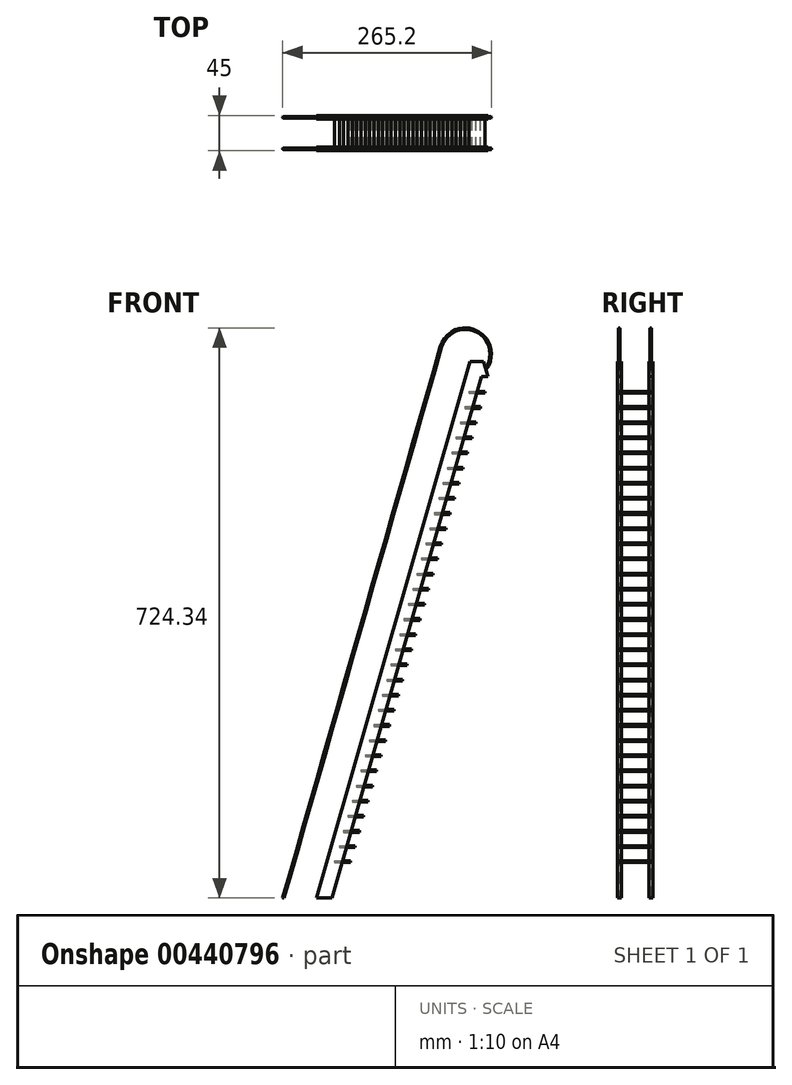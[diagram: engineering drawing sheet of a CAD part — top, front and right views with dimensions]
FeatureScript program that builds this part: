
annotation { "Feature Type Name" : "Feature", "Feature Type Description" : "" }
export const myFeature = defineFeature(function(context is Context, id is Id, definition is map)
    precondition{}
    {
        {
            var Q0;
            Q0=qCreatedBy(makeId("Front.planeOp"),FACE);
            cPlane(context, id + "F0", {"entities" : qUnion([Q0]), "cplaneType" : CPlaneType.OFFSET, "offset" : 20 * mm, "oppositeDirection" : true, "width" : 150 * mm, "height" : 150 * mm});
        }
        {
            var Q0;
            Q0=qCreatedBy(makeId("Front.planeOp"),FACE);
            var sketch = newSketch(context, id + "F1", { "sketchPlane" : qUnion([Q0])});
            skLineSegment(sketch, "E0.bottom", {"start": v(100, -350) * mm, "end": v(-100, -350) * mm});
            skLineSegment(sketch, "E0.top", {"start": v(100, 350) * mm, "end": v(-100, 350) * mm});
            skLineSegment(sketch, "E0.left", {"start": v(100, -350) * mm, "end": v(100, 350) * mm});
            skLineSegment(sketch, "E0.right", {"start": v(-100, -350) * mm, "end": v(-100, 350) * mm});
            skPoint(sketch, "E0.middle", {"position": v(0, 0) * mm});
            skSolve(sketch);
        }
        {
            var Q0;
            Q0=qCreatedBy(id+"F0.planeOp",FACE);
            var sketch = newSketch(context, id + "F2", { "sketchPlane" : qUnion([Q0])});
            skLineSegment(sketch, "E1.0", {"start": v(-100, -350) * mm, "end": v(-100, 350) * mm, "construction": true});
            skLineSegment(sketch, "E2.0", {"start": v(100, -350) * mm, "end": v(100, 350) * mm, "construction": true});
            skLineSegment(sketch, "E3.0", {"start": v(100, 350) * mm, "end": v(-100, 350) * mm, "construction": true});
            skLineSegment(sketch, "E4.0", {"start": v(100, -350) * mm, "end": v(-100, -350) * mm, "construction": true});
            skLineSegment(sketch, "E5", {"start": v(100, 350) * mm, "end": v(-100, -350) * mm});
            skLineSegment(sketch, "E6.0", {"start": v(128.85, 341.76) * mm, "end": v(-68.8, -350) * mm});
            skLineSegment(sketch, "E7", {"start": v(-100, -350) * mm, "end": v(-68.8, -350) * mm});
            skArc(sketch, "E8", {"start": v(157.14, 322.29) * mm, "mid": v(145.06, 370.15) * mm, "end": v(100, 350) * mm});
            skSolve(sketch);
        }
        {
            var Q0;
            Q0=qCreatedBy(makeId("Top.planeOp"),FACE);
            var Q1;
            Q1=sQuery(id+"F2.wireOp",VERTEX,"E7.start");
            cPlane(context, id + "F3", {"entities" : qUnion([Q0, Q1]), "cplaneType" : CPlaneType.PLANE_POINT, "offset" : 340.5 * mm, "oppositeDirection" : true, "width" : 150 * mm, "height" : 150 * mm});
        }
        {
            var Q0;
            Q0=qCreatedBy(id+"F3.planeOp",FACE);
            var sketch = newSketch(context, id + "F4", { "sketchPlane" : qUnion([Q0])});
            skPoint(sketch, "E9.0", {"position": v(-100, 20) * mm});
            skCircle(sketch, "E10", {"center": v(-100, 20) * mm, "radius": 1 * mm});
            skSolve(sketch);
        }
        {
            var Q0;
            Q0=makeQuery(id+"F4.imprint","IMPRINT",FACE,{"disambiguationData":[TD([[makeQuery(id+"F4.imprint","IMPRINT",EDGE,{"derivedFrom":sQuery(id+"F4.wireOp",EDGE,"E10")}),1.0]])]});
            var Q1;
            Q1=sQuery(id+"F2.wireOp",EDGE,"E5");
            var Q2;
            Q2=sQuery(id+"F2.wireOp",EDGE,"E8");
            sweep(context, id + "F5", {"profiles" : qUnion([Q0]), "path" : qUnion([Q1, Q2])});
        }
        {
            var Q0;
            Q0=qCreatedBy(id+"F0.planeOp",FACE);
            var sketch = newSketch(context, id + "F6", { "sketchPlane" : qUnion([Q0])});
            skPoint(sketch, "E11.0", {"position": v(157.14, 322.29) * mm});
            skPoint(sketch, "E12.0", {"position": v(100, 350) * mm});
            skPoint(sketch, "E13.0", {"position": v(-100, -350) * mm});
            skLineSegment(sketch, "E14.0", {"start": v(144.08, 322.29) * mm, "end": v(-48, -350) * mm});
            skLineSegment(sketch, "E15", {"start": v(157.14, 322.29) * mm, "end": v(144.08, 322.29) * mm});
            skLineSegment(sketch, "E16.0", {"start": v(100, -350) * mm, "end": v(-100, -350) * mm, "construction": true});
            skSolve(sketch);
        }
        {
            var Q0;
            Q0=qCreatedBy(id+"F3.planeOp",FACE);
            var sketch = newSketch(context, id + "F7", { "sketchPlane" : qUnion([Q0])});
            skLineSegment(sketch, "E17.bottom", {"start": v(-38, 22.5) * mm, "end": v(-58, 22.5) * mm});
            skLineSegment(sketch, "E17.top", {"start": v(-38, 17.5) * mm, "end": v(-58, 17.5) * mm});
            skLineSegment(sketch, "E17.left", {"start": v(-38, 22.5) * mm, "end": v(-38, 17.5) * mm});
            skLineSegment(sketch, "E17.right", {"start": v(-58, 22.5) * mm, "end": v(-58, 17.5) * mm});
            skPoint(sketch, "E17.middle", {"position": v(-48, 20) * mm});
            skSolve(sketch);
        }
        {
            var Q0;
            Q0 = qSketchRegion(id + "F7", true);
            var Q1;
            Q1=sQuery(id+"F6.wireOp",EDGE,"E14.0");
            var Q2;
            Q2=sQuery(id+"F6.wireOp",EDGE,"E15");
            sweep(context, id + "F8", {"profiles" : qUnion([Q0]), "path" : qUnion([Q1, Q2])});
        }
        {
            var Q0;
            Q0=makeQuery(id+"F5.opSweep","SWEPT_BODY",BODY,{"disambiguationData":[OSD([sQuery(id+"F2.wireOp",EDGE,"E8"),sQuery(id+"F4.wireOp",EDGE,"E10")])]});
            var Q1;
            Q1=makeQuery(id+"F8.opSweep","SWEPT_BODY",BODY,{"disambiguationData":[OSD([sQuery(id+"F6.wireOp",EDGE,"E15"),sQuery(id+"F7.wireOp",EDGE,"E17.bottom"),sQuery(id+"F7.wireOp",EDGE,"E17.top"),sQuery(id+"F7.wireOp",EDGE,"E17.left"),sQuery(id+"F7.wireOp",EDGE,"E17.right")])]});
            var Q2;
            Q2=makeQuery(id+"F1.imprint","IMPRINT",FACE,{"disambiguationData":[TD([[makeQuery(id+"F1.imprint","IMPRINT",EDGE,{"derivedFrom":sQuery(id+"F1.wireOp",EDGE,"E0.bottom")}),-1.0]])]});
            mirror(context, id + "F9", {"entities" : qUnion([Q0, Q1]), "mirrorPlane" : qUnion([Q2])});
        }
        {
            var Q0;
            Q0=qCreatedBy(id+"F0.planeOp",FACE);
            var sketch = newSketch(context, id + "F10", { "sketchPlane" : qUnion([Q0])});
            skLineSegment(sketch, "E18.0", {"start": v(144.08, 322.29) * mm, "end": v(-48, -350) * mm, "construction": true});
            skLineSegment(sketch, "E19.bottom", {"start": v(135.84, 293.44) * mm, "end": v(155.84, 293.44) * mm});
            skLineSegment(sketch, "E19.top", {"start": v(135.84, 291.44) * mm, "end": v(155.84, 291.44) * mm});
            skLineSegment(sketch, "E19.left", {"start": v(135.84, 293.44) * mm, "end": v(135.84, 291.44) * mm});
            skLineSegment(sketch, "E19.right", {"start": v(155.84, 293.44) * mm, "end": v(155.84, 291.44) * mm});
            skLineSegment(sketch, "E20.bottom", {"start": v(130.35, 274.21) * mm, "end": v(150.35, 274.21) * mm});
            skLineSegment(sketch, "E20.top", {"start": v(130.35, 272.21) * mm, "end": v(150.35, 272.21) * mm});
            skLineSegment(sketch, "E20.left", {"start": v(130.35, 274.21) * mm, "end": v(130.35, 272.21) * mm});
            skLineSegment(sketch, "E20.right", {"start": v(150.35, 274.21) * mm, "end": v(150.35, 272.21) * mm});
            skLineSegment(sketch, "E21.bottom", {"start": v(124.85, 254.98) * mm, "end": v(144.85, 254.98) * mm});
            skLineSegment(sketch, "E21.top", {"start": v(124.85, 252.98) * mm, "end": v(144.85, 252.98) * mm});
            skLineSegment(sketch, "E21.left", {"start": v(124.85, 254.98) * mm, "end": v(124.85, 252.98) * mm});
            skLineSegment(sketch, "E21.right", {"start": v(144.85, 254.98) * mm, "end": v(144.85, 252.98) * mm});
            skLineSegment(sketch, "E22.bottom", {"start": v(119.36, 235.75) * mm, "end": v(139.36, 235.75) * mm});
            skLineSegment(sketch, "E22.top", {"start": v(119.36, 233.75) * mm, "end": v(139.36, 233.75) * mm});
            skLineSegment(sketch, "E22.left", {"start": v(119.36, 235.75) * mm, "end": v(119.36, 233.75) * mm});
            skLineSegment(sketch, "E22.right", {"start": v(139.36, 235.75) * mm, "end": v(139.36, 233.75) * mm});
            skLineSegment(sketch, "E23.bottom", {"start": v(113.86, 216.52) * mm, "end": v(133.86, 216.52) * mm});
            skLineSegment(sketch, "E23.top", {"start": v(113.86, 214.52) * mm, "end": v(133.86, 214.52) * mm});
            skLineSegment(sketch, "E23.left", {"start": v(113.86, 216.52) * mm, "end": v(113.86, 214.52) * mm});
            skLineSegment(sketch, "E23.right", {"start": v(133.86, 216.52) * mm, "end": v(133.86, 214.52) * mm});
            skLineSegment(sketch, "E24.bottom", {"start": v(108.37, 197.29) * mm, "end": v(128.37, 197.29) * mm});
            skLineSegment(sketch, "E24.top", {"start": v(108.37, 195.29) * mm, "end": v(128.37, 195.29) * mm});
            skLineSegment(sketch, "E24.left", {"start": v(108.37, 197.29) * mm, "end": v(108.37, 195.29) * mm});
            skLineSegment(sketch, "E24.right", {"start": v(128.37, 197.29) * mm, "end": v(128.37, 195.29) * mm});
            skLineSegment(sketch, "E25.bottom", {"start": v(102.87, 178.06) * mm, "end": v(122.87, 178.06) * mm});
            skLineSegment(sketch, "E25.top", {"start": v(102.87, 176.06) * mm, "end": v(122.87, 176.06) * mm});
            skLineSegment(sketch, "E25.left", {"start": v(102.87, 178.06) * mm, "end": v(102.87, 176.06) * mm});
            skLineSegment(sketch, "E25.right", {"start": v(122.87, 178.06) * mm, "end": v(122.87, 176.06) * mm});
            skLineSegment(sketch, "E26.bottom", {"start": v(97.38, 158.83) * mm, "end": v(117.38, 158.83) * mm});
            skLineSegment(sketch, "E26.top", {"start": v(97.38, 156.83) * mm, "end": v(117.38, 156.83) * mm});
            skLineSegment(sketch, "E26.left", {"start": v(97.38, 158.83) * mm, "end": v(97.38, 156.83) * mm});
            skLineSegment(sketch, "E26.right", {"start": v(117.38, 158.83) * mm, "end": v(117.38, 156.83) * mm});
            skLineSegment(sketch, "E27.bottom", {"start": v(91.89, 139.6) * mm, "end": v(111.89, 139.6) * mm});
            skLineSegment(sketch, "E27.top", {"start": v(91.89, 137.6) * mm, "end": v(111.89, 137.6) * mm});
            skLineSegment(sketch, "E27.left", {"start": v(91.89, 139.6) * mm, "end": v(91.89, 137.6) * mm});
            skLineSegment(sketch, "E27.right", {"start": v(111.89, 139.6) * mm, "end": v(111.89, 137.6) * mm});
            skLineSegment(sketch, "E28.bottom", {"start": v(86.4, 120.37) * mm, "end": v(106.4, 120.37) * mm});
            skLineSegment(sketch, "E28.top", {"start": v(86.4, 118.37) * mm, "end": v(106.4, 118.37) * mm});
            skLineSegment(sketch, "E28.left", {"start": v(86.4, 120.37) * mm, "end": v(86.4, 118.37) * mm});
            skLineSegment(sketch, "E28.right", {"start": v(106.4, 120.37) * mm, "end": v(106.4, 118.37) * mm});
            skLineSegment(sketch, "E29.bottom", {"start": v(80.9, 101.14) * mm, "end": v(100.9, 101.14) * mm});
            skLineSegment(sketch, "E29.top", {"start": v(80.9, 99.14) * mm, "end": v(100.9, 99.14) * mm});
            skLineSegment(sketch, "E29.left", {"start": v(80.9, 101.14) * mm, "end": v(80.9, 99.14) * mm});
            skLineSegment(sketch, "E29.right", {"start": v(100.9, 101.14) * mm, "end": v(100.9, 99.14) * mm});
            skLineSegment(sketch, "E30.bottom", {"start": v(75.4, 81.9) * mm, "end": v(95.4, 81.9) * mm});
            skLineSegment(sketch, "E30.top", {"start": v(75.4, 79.9) * mm, "end": v(95.4, 79.9) * mm});
            skLineSegment(sketch, "E30.left", {"start": v(75.4, 81.9) * mm, "end": v(75.4, 79.9) * mm});
            skLineSegment(sketch, "E30.right", {"start": v(95.4, 81.9) * mm, "end": v(95.4, 79.9) * mm});
            skLineSegment(sketch, "E31.bottom", {"start": v(69.9, 62.68) * mm, "end": v(89.9, 62.68) * mm});
            skLineSegment(sketch, "E31.top", {"start": v(69.9, 60.68) * mm, "end": v(89.9, 60.68) * mm});
            skLineSegment(sketch, "E31.left", {"start": v(69.9, 62.68) * mm, "end": v(69.9, 60.68) * mm});
            skLineSegment(sketch, "E31.right", {"start": v(89.9, 62.68) * mm, "end": v(89.9, 60.68) * mm});
            skLineSegment(sketch, "E32.bottom", {"start": v(64.41, 43.45) * mm, "end": v(84.41, 43.45) * mm});
            skLineSegment(sketch, "E32.top", {"start": v(64.41, 41.45) * mm, "end": v(84.41, 41.45) * mm});
            skLineSegment(sketch, "E32.left", {"start": v(64.41, 43.45) * mm, "end": v(64.41, 41.45) * mm});
            skLineSegment(sketch, "E32.right", {"start": v(84.41, 43.45) * mm, "end": v(84.41, 41.45) * mm});
            skLineSegment(sketch, "E33.bottom", {"start": v(58.92, 24.21) * mm, "end": v(78.92, 24.21) * mm});
            skLineSegment(sketch, "E33.top", {"start": v(58.92, 22.21) * mm, "end": v(78.92, 22.21) * mm});
            skLineSegment(sketch, "E33.left", {"start": v(58.92, 24.21) * mm, "end": v(58.92, 22.21) * mm});
            skLineSegment(sketch, "E33.right", {"start": v(78.92, 24.21) * mm, "end": v(78.92, 22.21) * mm});
            skLineSegment(sketch, "E34.bottom", {"start": v(53.42, 4.98) * mm, "end": v(73.42, 4.98) * mm});
            skLineSegment(sketch, "E34.top", {"start": v(53.42, 2.98) * mm, "end": v(73.42, 2.98) * mm});
            skLineSegment(sketch, "E34.left", {"start": v(53.42, 4.98) * mm, "end": v(53.42, 2.98) * mm});
            skLineSegment(sketch, "E34.right", {"start": v(73.42, 4.98) * mm, "end": v(73.42, 2.98) * mm});
            skLineSegment(sketch, "E35.bottom", {"start": v(47.93, -14.25) * mm, "end": v(67.93, -14.25) * mm});
            skLineSegment(sketch, "E35.top", {"start": v(47.93, -16.25) * mm, "end": v(67.93, -16.25) * mm});
            skLineSegment(sketch, "E35.left", {"start": v(47.93, -14.25) * mm, "end": v(47.93, -16.25) * mm});
            skLineSegment(sketch, "E35.right", {"start": v(67.93, -14.25) * mm, "end": v(67.93, -16.25) * mm});
            skLineSegment(sketch, "E36.bottom", {"start": v(42.44, -33.48) * mm, "end": v(62.44, -33.48) * mm});
            skLineSegment(sketch, "E36.top", {"start": v(42.44, -35.48) * mm, "end": v(62.44, -35.48) * mm});
            skLineSegment(sketch, "E36.left", {"start": v(42.44, -33.48) * mm, "end": v(42.44, -35.48) * mm});
            skLineSegment(sketch, "E36.right", {"start": v(62.44, -33.48) * mm, "end": v(62.44, -35.48) * mm});
            skLineSegment(sketch, "E37.bottom", {"start": v(36.94, -52.7) * mm, "end": v(56.94, -52.7) * mm});
            skLineSegment(sketch, "E37.top", {"start": v(36.94, -54.7) * mm, "end": v(56.94, -54.7) * mm});
            skLineSegment(sketch, "E37.left", {"start": v(36.94, -52.7) * mm, "end": v(36.94, -54.7) * mm});
            skLineSegment(sketch, "E37.right", {"start": v(56.94, -52.7) * mm, "end": v(56.94, -54.7) * mm});
            skLineSegment(sketch, "E38.bottom", {"start": v(31.45, -71.94) * mm, "end": v(51.45, -71.94) * mm});
            skLineSegment(sketch, "E38.top", {"start": v(31.45, -73.94) * mm, "end": v(51.45, -73.94) * mm});
            skLineSegment(sketch, "E38.left", {"start": v(31.45, -71.94) * mm, "end": v(31.45, -73.94) * mm});
            skLineSegment(sketch, "E38.right", {"start": v(51.45, -71.94) * mm, "end": v(51.45, -73.94) * mm});
            skLineSegment(sketch, "E39.bottom", {"start": v(25.95, -91.17) * mm, "end": v(45.95, -91.17) * mm});
            skLineSegment(sketch, "E39.top", {"start": v(25.95, -93.17) * mm, "end": v(45.95, -93.17) * mm});
            skLineSegment(sketch, "E39.left", {"start": v(25.95, -91.17) * mm, "end": v(25.95, -93.17) * mm});
            skLineSegment(sketch, "E39.right", {"start": v(45.95, -91.17) * mm, "end": v(45.95, -93.17) * mm});
            skLineSegment(sketch, "E40.bottom", {"start": v(20.46, -110.4) * mm, "end": v(40.46, -110.4) * mm});
            skLineSegment(sketch, "E40.top", {"start": v(20.46, -112.4) * mm, "end": v(40.46, -112.4) * mm});
            skLineSegment(sketch, "E40.left", {"start": v(20.46, -110.4) * mm, "end": v(20.46, -112.4) * mm});
            skLineSegment(sketch, "E40.right", {"start": v(40.46, -110.4) * mm, "end": v(40.46, -112.4) * mm});
            skLineSegment(sketch, "E41.bottom", {"start": v(14.96, -129.63) * mm, "end": v(34.96, -129.63) * mm});
            skLineSegment(sketch, "E41.top", {"start": v(14.96, -131.63) * mm, "end": v(34.96, -131.63) * mm});
            skLineSegment(sketch, "E41.left", {"start": v(14.96, -129.63) * mm, "end": v(14.96, -131.63) * mm});
            skLineSegment(sketch, "E41.right", {"start": v(34.96, -129.63) * mm, "end": v(34.96, -131.63) * mm});
            skLineSegment(sketch, "E42.bottom", {"start": v(9.47, -148.86) * mm, "end": v(29.47, -148.86) * mm});
            skLineSegment(sketch, "E42.top", {"start": v(9.47, -150.86) * mm, "end": v(29.47, -150.86) * mm});
            skLineSegment(sketch, "E42.left", {"start": v(9.47, -148.86) * mm, "end": v(9.47, -150.86) * mm});
            skLineSegment(sketch, "E42.right", {"start": v(29.47, -148.86) * mm, "end": v(29.47, -150.86) * mm});
            skLineSegment(sketch, "E43.bottom", {"start": v(3.98, -168.09) * mm, "end": v(23.98, -168.09) * mm});
            skLineSegment(sketch, "E43.top", {"start": v(3.98, -170.09) * mm, "end": v(23.98, -170.09) * mm});
            skLineSegment(sketch, "E43.left", {"start": v(3.98, -168.09) * mm, "end": v(3.98, -170.09) * mm});
            skLineSegment(sketch, "E43.right", {"start": v(23.98, -168.09) * mm, "end": v(23.98, -170.09) * mm});
            skLineSegment(sketch, "E44.bottom", {"start": v(-1.52, -187.32) * mm, "end": v(18.48, -187.32) * mm});
            skLineSegment(sketch, "E44.top", {"start": v(-1.52, -189.32) * mm, "end": v(18.48, -189.32) * mm});
            skLineSegment(sketch, "E44.left", {"start": v(-1.52, -187.32) * mm, "end": v(-1.52, -189.32) * mm});
            skLineSegment(sketch, "E44.right", {"start": v(18.48, -187.32) * mm, "end": v(18.48, -189.32) * mm});
            skLineSegment(sketch, "E45.bottom", {"start": v(-7.01, -206.55) * mm, "end": v(12.99, -206.55) * mm});
            skLineSegment(sketch, "E45.top", {"start": v(-7.01, -208.55) * mm, "end": v(12.99, -208.55) * mm});
            skLineSegment(sketch, "E45.left", {"start": v(-7.01, -206.55) * mm, "end": v(-7.01, -208.55) * mm});
            skLineSegment(sketch, "E45.right", {"start": v(12.99, -206.55) * mm, "end": v(12.99, -208.55) * mm});
            skLineSegment(sketch, "E46.bottom", {"start": v(-12.5, -225.78) * mm, "end": v(7.5, -225.78) * mm});
            skLineSegment(sketch, "E46.top", {"start": v(-12.5, -227.78) * mm, "end": v(7.5, -227.78) * mm});
            skLineSegment(sketch, "E46.left", {"start": v(-12.5, -225.78) * mm, "end": v(-12.5, -227.78) * mm});
            skLineSegment(sketch, "E46.right", {"start": v(7.5, -225.78) * mm, "end": v(7.5, -227.78) * mm});
            skLineSegment(sketch, "E47.bottom", {"start": v(-18, -245.01) * mm, "end": v(2, -245.01) * mm});
            skLineSegment(sketch, "E47.top", {"start": v(-18, -247.01) * mm, "end": v(2, -247.01) * mm});
            skLineSegment(sketch, "E47.left", {"start": v(-18, -245.01) * mm, "end": v(-18, -247.01) * mm});
            skLineSegment(sketch, "E47.right", {"start": v(2, -245.01) * mm, "end": v(2, -247.01) * mm});
            skLineSegment(sketch, "E48.bottom", {"start": v(-23.5, -264.24) * mm, "end": v(-3.5, -264.24) * mm});
            skLineSegment(sketch, "E48.top", {"start": v(-23.5, -266.24) * mm, "end": v(-3.5, -266.24) * mm});
            skLineSegment(sketch, "E48.left", {"start": v(-23.5, -264.24) * mm, "end": v(-23.5, -266.24) * mm});
            skLineSegment(sketch, "E48.right", {"start": v(-3.5, -264.24) * mm, "end": v(-3.5, -266.24) * mm});
            skLineSegment(sketch, "E49.bottom", {"start": v(-29, -283.47) * mm, "end": v(-9, -283.47) * mm});
            skLineSegment(sketch, "E49.top", {"start": v(-29, -285.47) * mm, "end": v(-9, -285.47) * mm});
            skLineSegment(sketch, "E49.left", {"start": v(-29, -283.47) * mm, "end": v(-29, -285.47) * mm});
            skLineSegment(sketch, "E49.right", {"start": v(-9, -283.47) * mm, "end": v(-9, -285.47) * mm});
            skLineSegment(sketch, "E50.bottom", {"start": v(-35.01, -302.55) * mm, "end": v(-15.01, -302.55) * mm});
            skLineSegment(sketch, "E50.top", {"start": v(-35.01, -304.55) * mm, "end": v(-15.01, -304.55) * mm});
            skLineSegment(sketch, "E50.left", {"start": v(-35.01, -302.55) * mm, "end": v(-35.01, -304.55) * mm});
            skLineSegment(sketch, "E50.right", {"start": v(-15.01, -302.55) * mm, "end": v(-15.01, -304.55) * mm});
            skSolve(sketch);
        }
        {
            var Q0;
            Q0 = qSketchRegion(id + "F10", true);
            extrude(context, id + "F11", {"entities" : qUnion([Q0]), "depth" : 40 * mm});
        }
    });
